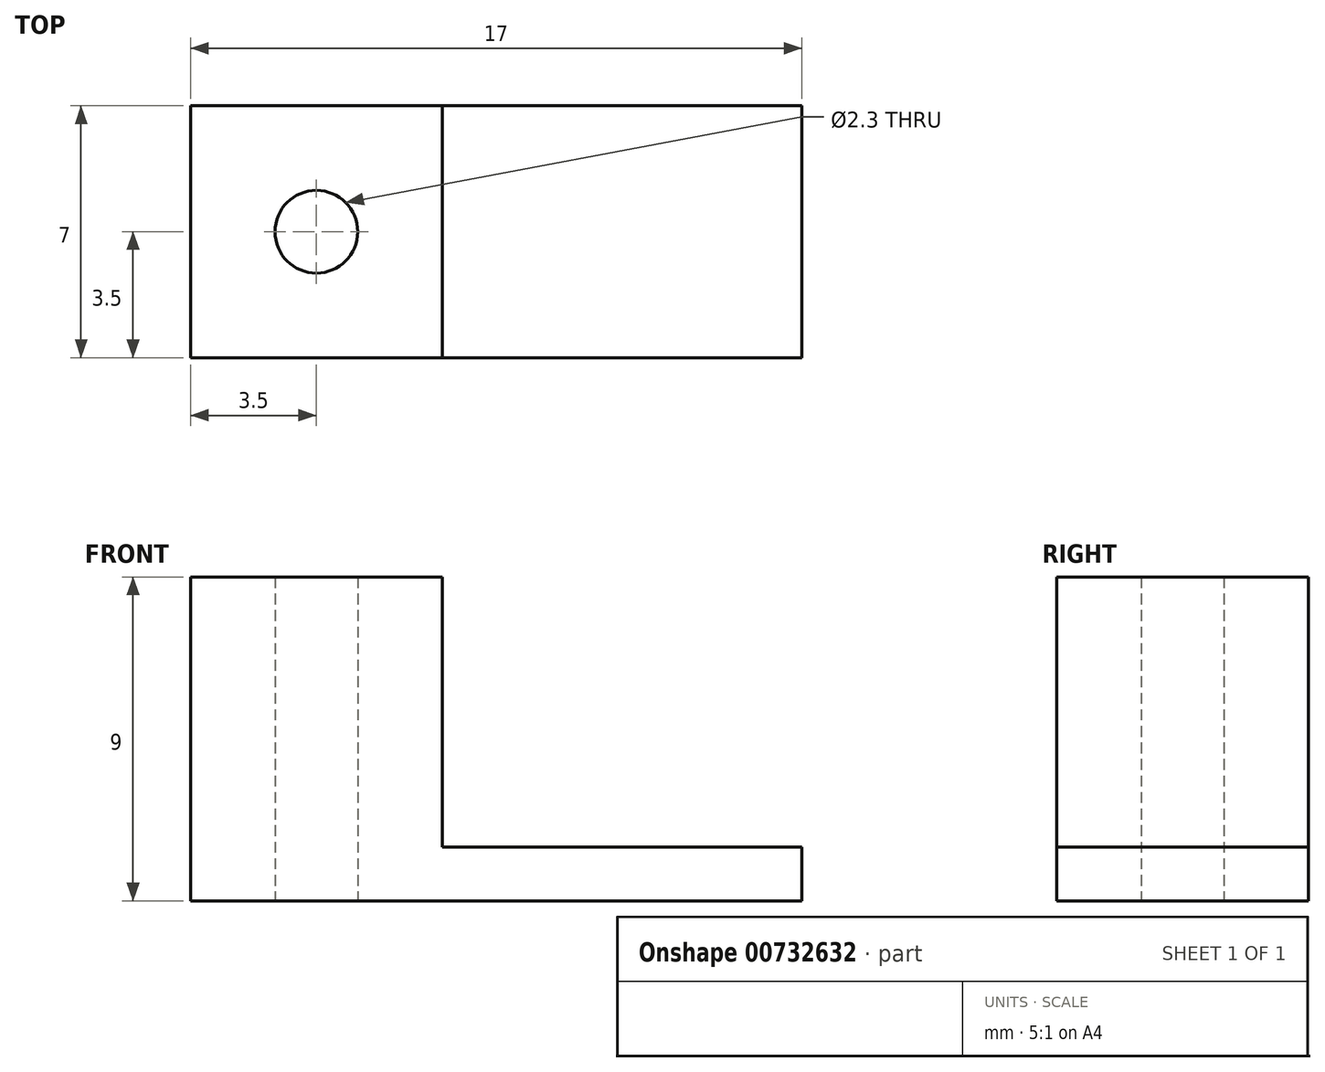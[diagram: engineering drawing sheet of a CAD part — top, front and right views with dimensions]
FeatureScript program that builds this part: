
annotation { "Feature Type Name" : "Feature", "Feature Type Description" : "" }
export const myFeature = defineFeature(function(context is Context, id is Id, definition is map)
    precondition{}
    {
        {
            var Q0;
            Q0=qCreatedBy(makeId("Top.planeOp"),FACE);
            var sketch = newSketch(context, id + "F0", { "sketchPlane" : qUnion([Q0])});
            skLineSegment(sketch, "E0.bottom", {"start": v(3.5, 3.5) * mm, "end": v(-3.5, 3.5) * mm});
            skLineSegment(sketch, "E0.top", {"start": v(3.5, -3.5) * mm, "end": v(-3.5, -3.5) * mm});
            skLineSegment(sketch, "E0.left", {"start": v(3.5, 3.5) * mm, "end": v(3.5, -3.5) * mm});
            skLineSegment(sketch, "E0.right", {"start": v(-3.5, 3.5) * mm, "end": v(-3.5, -3.5) * mm});
            skPoint(sketch, "E0.middle", {"position": v(0, 0) * mm});
            skCircle(sketch, "E1", {"center": v(0, 0) * mm, "radius": 1.15 * mm});
            skSolve(sketch);
        }
        {
            var Q0;
            Q0=makeQuery(id+"F0.imprint","IMPRINT",FACE,{"disambiguationData":[TD([[makeQuery(id+"F0.imprint","IMPRINT",EDGE,{"derivedFrom":sQuery(id+"F0.wireOp",EDGE,"E0.bottom")}),1.0]])]});
            extrude(context, id + "F1", {"entities" : qUnion([Q0]), "endBound" : BoundingType.SYMMETRIC, "depth" : 9 * mm, "offsetDistance" : 25 * mm});
        }
        {
            var Q0;
            Q0=makeQuery(id+"F1.opExtrude","SWEPT_FACE",FACE,{"disambiguationData":[OSD([sQuery(id+"F0.wireOp",EDGE,"E0.left")])]});
            var sketch = newSketch(context, id + "F2", { "sketchPlane" : qUnion([Q0])});
            skLineSegment(sketch, "E2", {"start": v(-3.5, -3) * mm, "end": v(3.5, -3) * mm});
            skSolve(sketch);
        }
        {
            var Q0;
            {var subQ0=sQuery(id+"F2.wireOp",EDGE,"E2");Q0=makeQuery(id+"F2.imprint","IMPRINT",FACE,{"disambiguationData":[TD([[makeQuery(id+"F2.imprint","IMPRINT",EDGE,{"derivedFrom":subQ0}),-1.0]])]});}
            extrude(context, id + "F3", {"entities" : qUnion([Q0]), "operationType" : NewBodyOperationType.ADD, "depth" : 10 * mm, "offsetDistance" : 25 * mm});
        }
    });
